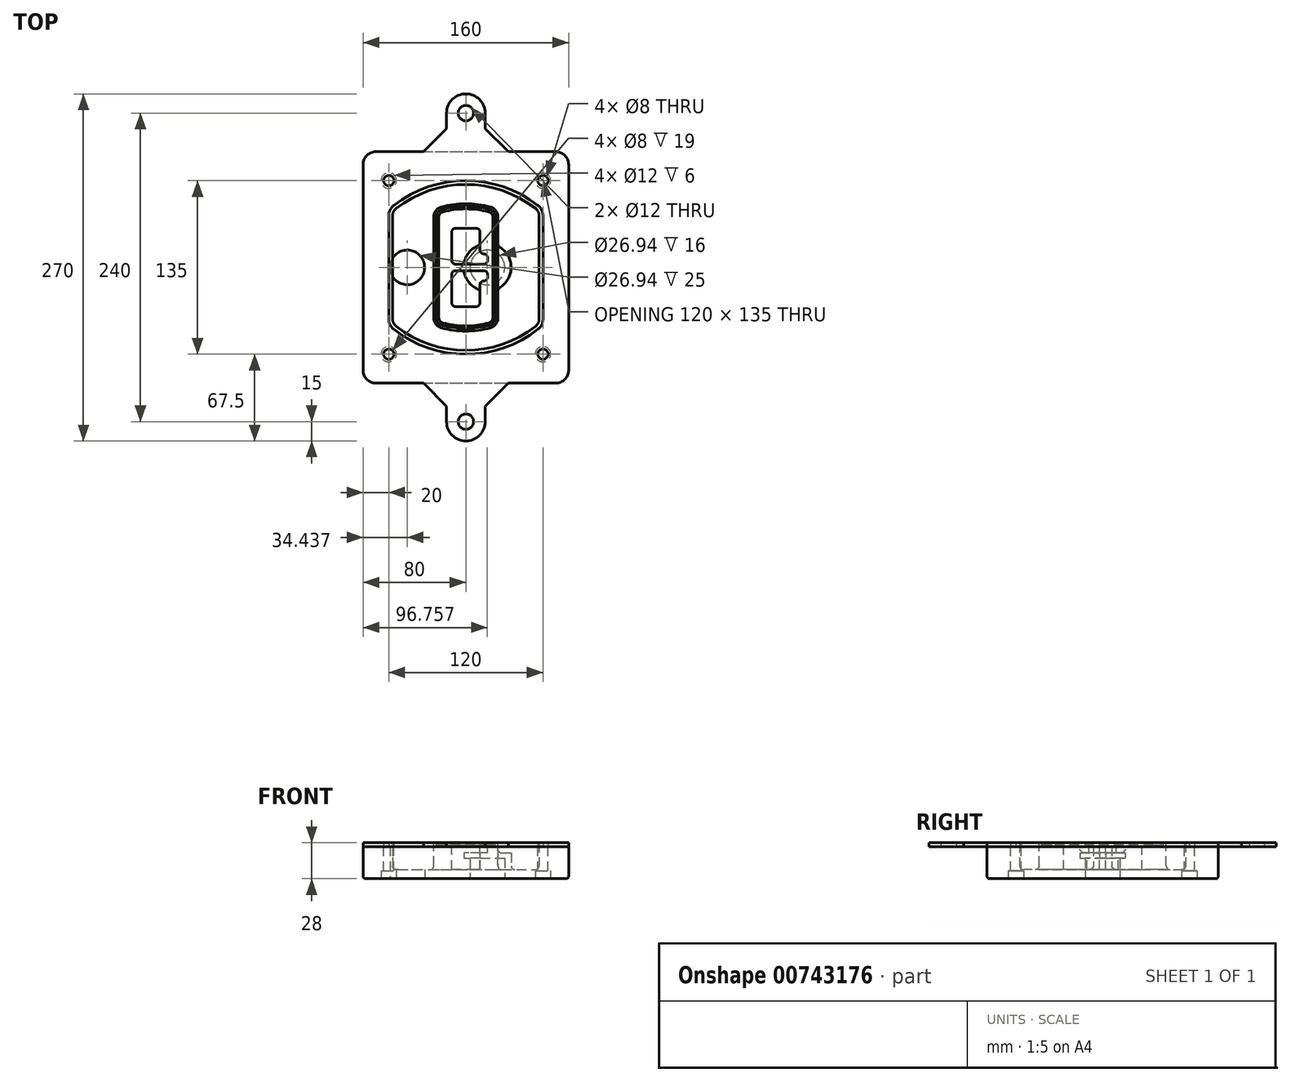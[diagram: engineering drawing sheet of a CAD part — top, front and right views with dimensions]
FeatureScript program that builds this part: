
annotation { "Feature Type Name" : "Feature", "Feature Type Description" : "" }
export const myFeature = defineFeature(function(context is Context, id is Id, definition is map)
    precondition{}
    {
        {
            var Q0;
            Q0=qCreatedBy(makeId("Top.planeOp"),FACE);
            var sketch = newSketch(context, id + "F0", { "sketchPlane" : qUnion([Q0])});
            skPoint(sketch, "E0.rect.middle", {"position": v(0, 0) * mm});
            skLineSegment(sketch, "E1.bottom", {"start": v(-70, -90) * mm, "end": v(70, -90) * mm});
            skLineSegment(sketch, "E1.top", {"start": v(-70, 90) * mm, "end": v(70, 90) * mm});
            skLineSegment(sketch, "E1.left", {"start": v(-80, -80) * mm, "end": v(-80, 80) * mm});
            skLineSegment(sketch, "E1.right", {"start": v(80, -80) * mm, "end": v(80, 80) * mm});
            skLineSegment(sketch, "E2", {"start": v(-80, 90) * mm, "end": v(80, -90) * mm, "construction": true});
            skLineSegment(sketch, "E3", {"start": v(80, 90) * mm, "end": v(-80, -90) * mm, "construction": true});
            skCircle(sketch, "E4", {"center": v(-60, 67.5) * mm, "radius": 4 * mm});
            skCircle(sketch, "E5", {"center": v(60, 67.5) * mm, "radius": 4 * mm});
            skCircle(sketch, "E6", {"center": v(60, -67.5) * mm, "radius": 4 * mm});
            skCircle(sketch, "E7", {"center": v(-60, -67.5) * mm, "radius": 4 * mm});
            skLineSegment(sketch, "E8", {"start": v(-60, 67.5) * mm, "end": v(60, 67.5) * mm, "construction": true});
            skLineSegment(sketch, "E9", {"start": v(60, 67.5) * mm, "end": v(60, -67.5) * mm, "construction": true});
            skLineSegment(sketch, "E10", {"start": v(60, -67.5) * mm, "end": v(-60, -67.5) * mm, "construction": true});
            skLineSegment(sketch, "E11", {"start": v(-60, -67.5) * mm, "end": v(-60, 67.5) * mm, "construction": true});
            skLineSegment(sketch, "E12", {"start": v(-60, 40.3) * mm, "end": v(-60, -40.3) * mm});
            skLineSegment(sketch, "E13", {"start": v(60, 40.3) * mm, "end": v(60, -40.3) * mm});
            skArc(sketch, "E14", {"start": v(56.15, 48.18) * mm, "mid": v(0, 67.5) * mm, "end": v(-56.15, 48.18) * mm});
            skArc(sketch, "E15", {"start": v(-56.15, -48.18) * mm, "mid": v(0, -67.5) * mm, "end": v(56.15, -48.18) * mm});
            skLineSegment(sketch, "E16", {"start": v(-60, 0) * mm, "end": v(60, 0) * mm, "construction": true});
            skPoint(sketch, "E17.visualSharp", {"position": v(-60, -45) * mm});
            skArc(sketch, "E17.filletArc", {"start": v(-60, -40.3) * mm, "mid": v(-58.99, -44.68) * mm, "end": v(-56.15, -48.18) * mm});
            skPoint(sketch, "E18.visualSharp", {"position": v(-60, 45) * mm});
            skArc(sketch, "E18.filletArc", {"start": v(-56.15, 48.18) * mm, "mid": v(-58.99, 44.68) * mm, "end": v(-60, 40.3) * mm});
            skPoint(sketch, "E19.visualSharp", {"position": v(60, 45) * mm});
            skArc(sketch, "E19.filletArc", {"start": v(60, 40.3) * mm, "mid": v(58.99, 44.68) * mm, "end": v(56.15, 48.18) * mm});
            skPoint(sketch, "E20.visualSharp", {"position": v(60, -45) * mm});
            skArc(sketch, "E20.filletArc", {"start": v(56.15, -48.18) * mm, "mid": v(58.99, -44.68) * mm, "end": v(60, -40.3) * mm});
            skPoint(sketch, "E21.visualSharp", {"position": v(-80, 90) * mm});
            skArc(sketch, "E21.filletArc", {"start": v(-70, 90) * mm, "mid": v(-77.07, 87.07) * mm, "end": v(-80, 80) * mm});
            skPoint(sketch, "E22.visualSharp", {"position": v(80, 90) * mm});
            skArc(sketch, "E22.filletArc", {"start": v(80, 80) * mm, "mid": v(77.07, 87.07) * mm, "end": v(70, 90) * mm});
            skPoint(sketch, "E23.visualSharp", {"position": v(80, -90) * mm});
            skArc(sketch, "E23.filletArc", {"start": v(70, -90) * mm, "mid": v(77.07, -87.07) * mm, "end": v(80, -80) * mm});
            skPoint(sketch, "E24.visualSharp", {"position": v(-80, -90) * mm});
            skArc(sketch, "E24.filletArc", {"start": v(-80, -80) * mm, "mid": v(-77.07, -87.07) * mm, "end": v(-70, -90) * mm});
            skArc(sketch, "E25.0", {"start": v(57, 40.3) * mm, "mid": v(56.3, 43.36) * mm, "end": v(54.3, 45.81) * mm});
            skLineSegment(sketch, "E25.1", {"start": v(57, 40.3) * mm, "end": v(57, -40.3) * mm});
            skArc(sketch, "E25.2", {"start": v(54.3, -45.81) * mm, "mid": v(56.3, -43.36) * mm, "end": v(57, -40.3) * mm});
            skArc(sketch, "E25.3", {"start": v(-54.3, -45.81) * mm, "mid": v(0, -64.5) * mm, "end": v(54.3, -45.81) * mm});
            skArc(sketch, "E25.4", {"start": v(-57, -40.3) * mm, "mid": v(-56.3, -43.36) * mm, "end": v(-54.3, -45.81) * mm});
            skArc(sketch, "E25.5", {"start": v(54.3, 45.81) * mm, "mid": v(0, 64.5) * mm, "end": v(-54.3, 45.81) * mm});
            skLineSegment(sketch, "E25.6", {"start": v(-57, 40.3) * mm, "end": v(-57, -40.3) * mm});
            skArc(sketch, "E25.7", {"start": v(-54.3, 45.81) * mm, "mid": v(-56.3, 43.36) * mm, "end": v(-57, 40.3) * mm});
            skArc(sketch, "E26.0", {"start": v(-58.62, 51.33) * mm, "mid": v(-62.58, 46.43) * mm, "end": v(-64, 40.3) * mm});
            skArc(sketch, "E26.1", {"start": v(58.62, 51.33) * mm, "mid": v(0, 71.5) * mm, "end": v(-58.62, 51.33) * mm});
            skArc(sketch, "E26.2", {"start": v(64, 40.3) * mm, "mid": v(62.58, 46.43) * mm, "end": v(58.62, 51.33) * mm});
            skLineSegment(sketch, "E26.3", {"start": v(64, 40.3) * mm, "end": v(64, -40.3) * mm});
            skArc(sketch, "E26.4", {"start": v(58.62, -51.33) * mm, "mid": v(62.58, -46.43) * mm, "end": v(64, -40.3) * mm});
            skLineSegment(sketch, "E26.5", {"start": v(-64, 40.3) * mm, "end": v(-64, -40.3) * mm});
            skArc(sketch, "E26.6", {"start": v(-58.62, -51.33) * mm, "mid": v(0, -71.5) * mm, "end": v(58.62, -51.33) * mm});
            skArc(sketch, "E26.7", {"start": v(-64, -40.3) * mm, "mid": v(-62.58, -46.43) * mm, "end": v(-58.62, -51.33) * mm});
            skSolve(sketch);
        }
        {
            var Q0;
            Q0=makeQuery(id+"F0.imprint","IMPRINT",FACE,{"disambiguationData":[TD([[makeQuery(id+"F0.imprint","IMPRINT",EDGE,{"derivedFrom":sQuery(id+"F0.wireOp",EDGE,"E1.bottom")}),1.0]])]});
            var Q1;
            Q1=makeQuery(id+"F0.imprint","IMPRINT",FACE,{"disambiguationData":[TD([[makeQuery(id+"F0.imprint","IMPRINT",EDGE,{"derivedFrom":sQuery(id+"F0.wireOp",EDGE,"E12")}),1.0]])]});
            var Q2;
            Q2=makeQuery(id+"F0.imprint","IMPRINT",FACE,{"disambiguationData":[TD([[makeQuery(id+"F0.imprint","IMPRINT",EDGE,{"derivedFrom":sQuery(id+"F0.wireOp",EDGE,"E25.0")}),1.0]])]});
            var Q3;
            Q3=makeQuery(id+"F0.imprint","IMPRINT",FACE,{"disambiguationData":[TD([[makeQuery(id+"F0.imprint","IMPRINT",EDGE,{"derivedFrom":sQuery(id+"F0.wireOp",EDGE,"E12")}),-1.0]])]});
            extrude(context, id + "F1", {"entities" : qUnion([Q0, Q1, Q2, Q3]), "oppositeDirection" : true, "depth" : 25 * mm});
        }
        {
            var Q0;
            Q0=makeQuery(id+"F0.imprint","IMPRINT",FACE,{"disambiguationData":[TD([[makeQuery(id+"F0.imprint","IMPRINT",EDGE,{"derivedFrom":sQuery(id+"F0.wireOp",EDGE,"E12")}),1.0]])]});
            extrude(context, id + "F2", {"entities" : qUnion([Q0]), "operationType" : NewBodyOperationType.ADD, "depth" : 3 * mm});
        }
        {
            var Q0;
            Q0=makeQuery(id+"F0.imprint","IMPRINT",FACE,{"disambiguationData":[TD([[makeQuery(id+"F0.imprint","IMPRINT",EDGE,{"derivedFrom":sQuery(id+"F0.wireOp",EDGE,"E25.0")}),1.0]])]});
            extrude(context, id + "F3", {"entities" : qUnion([Q0]), "operationType" : NewBodyOperationType.REMOVE, "oppositeDirection" : true, "depth" : 18 * mm});
        }
        {
            var Q0;
            Q0=makeQuery(id+"F2.opExtrude","CAP_FACE",FACE,{"disambiguationData":[OSD([sQuery(id+"F0.wireOp",EDGE,"E12"),sQuery(id+"F0.wireOp",EDGE,"E13"),sQuery(id+"F0.wireOp",EDGE,"E14"),sQuery(id+"F0.wireOp",EDGE,"E15"),sQuery(id+"F0.wireOp",EDGE,"E17.filletArc"),sQuery(id+"F0.wireOp",EDGE,"E18.filletArc"),sQuery(id+"F0.wireOp",EDGE,"E19.filletArc"),sQuery(id+"F0.wireOp",EDGE,"E20.filletArc"),sQuery(id+"F0.wireOp",EDGE,"E25.0"),sQuery(id+"F0.wireOp",EDGE,"E25.1"),sQuery(id+"F0.wireOp",EDGE,"E25.2"),sQuery(id+"F0.wireOp",EDGE,"E25.3"),sQuery(id+"F0.wireOp",EDGE,"E25.4"),sQuery(id+"F0.wireOp",EDGE,"E25.5"),sQuery(id+"F0.wireOp",EDGE,"E25.6"),sQuery(id+"F0.wireOp",EDGE,"E25.7")])],"isStart":false});
            var sketch = newSketch(context, id + "F4", { "sketchPlane" : qUnion([Q0])});
            skArc(sketch, "E27.0", {"start": v(-19.08, -46.97) * mm, "mid": v(0, -49.5) * mm, "end": v(19.08, -46.97) * mm});
            skArc(sketch, "E28.0", {"start": v(19.08, 46.97) * mm, "mid": v(0, 49.5) * mm, "end": v(-19.08, 46.97) * mm});
            skLineSegment(sketch, "E29", {"start": v(-25, 39.25) * mm, "end": v(-25, -39.25) * mm});
            skLineSegment(sketch, "E30", {"start": v(25, 39.25) * mm, "end": v(25, -39.25) * mm});
            skLineSegment(sketch, "E31", {"start": v(-25, 45.1) * mm, "end": v(25, 45.1) * mm, "construction": true});
            skLineSegment(sketch, "E32", {"start": v(-25, -45.1) * mm, "end": v(25, -45.1) * mm, "construction": true});
            skPoint(sketch, "E33.visualSharp", {"position": v(-25, 45.1) * mm});
            skArc(sketch, "E33.filletArc", {"start": v(-19.08, 46.97) * mm, "mid": v(-23.35, 44.11) * mm, "end": v(-25, 39.25) * mm});
            skPoint(sketch, "E34.visualSharp", {"position": v(25, 45.1) * mm});
            skArc(sketch, "E34.filletArc", {"start": v(25, 39.25) * mm, "mid": v(23.35, 44.11) * mm, "end": v(19.08, 46.97) * mm});
            skPoint(sketch, "E35.visualSharp", {"position": v(25, -45.1) * mm});
            skArc(sketch, "E35.filletArc", {"start": v(19.08, -46.97) * mm, "mid": v(23.35, -44.11) * mm, "end": v(25, -39.25) * mm});
            skPoint(sketch, "E36.visualSharp", {"position": v(-25, -45.1) * mm});
            skArc(sketch, "E36.filletArc", {"start": v(-25, -39.25) * mm, "mid": v(-23.35, -44.11) * mm, "end": v(-19.08, -46.97) * mm});
            skArc(sketch, "E37.0", {"start": v(54.3, 45.81) * mm, "mid": v(0, 64.5) * mm, "end": v(-54.3, 45.81) * mm});
            skArc(sketch, "E37.1", {"start": v(-54.3, 45.81) * mm, "mid": v(-56.3, 43.36) * mm, "end": v(-57, 40.3) * mm});
            skLineSegment(sketch, "E37.2", {"start": v(-57, 40.3) * mm, "end": v(-57, -40.3) * mm});
            skArc(sketch, "E37.3", {"start": v(-57, -40.3) * mm, "mid": v(-56.3, -43.36) * mm, "end": v(-54.3, -45.81) * mm});
            skArc(sketch, "E37.4", {"start": v(-54.3, -45.81) * mm, "mid": v(0, -64.5) * mm, "end": v(54.3, -45.81) * mm});
            skArc(sketch, "E37.5", {"start": v(54.3, -45.81) * mm, "mid": v(56.3, -43.36) * mm, "end": v(57, -40.3) * mm});
            skLineSegment(sketch, "E37.6", {"start": v(57, 40.3) * mm, "end": v(57, -40.3) * mm});
            skArc(sketch, "E37.7", {"start": v(57, 40.3) * mm, "mid": v(56.3, 43.36) * mm, "end": v(54.3, 45.81) * mm});
            skLineSegment(sketch, "E38.0", {"start": v(23, 39.25) * mm, "end": v(23, -39.25) * mm});
            skArc(sketch, "E38.1", {"start": v(18.56, -45.04) * mm, "mid": v(21.76, -42.9) * mm, "end": v(23, -39.25) * mm});
            skArc(sketch, "E38.2", {"start": v(-18.56, -45.04) * mm, "mid": v(0, -47.5) * mm, "end": v(18.56, -45.04) * mm});
            skArc(sketch, "E38.3", {"start": v(-23, -39.25) * mm, "mid": v(-21.76, -42.9) * mm, "end": v(-18.56, -45.04) * mm});
            skLineSegment(sketch, "E38.4", {"start": v(-23, 39.25) * mm, "end": v(-23, -39.25) * mm});
            skArc(sketch, "E38.5", {"start": v(23, 39.25) * mm, "mid": v(21.76, 42.9) * mm, "end": v(18.56, 45.04) * mm});
            skArc(sketch, "E38.6", {"start": v(-18.56, 45.04) * mm, "mid": v(-21.76, 42.9) * mm, "end": v(-23, 39.25) * mm});
            skArc(sketch, "E38.7", {"start": v(18.56, 45.04) * mm, "mid": v(0, 47.5) * mm, "end": v(-18.56, 45.04) * mm});
            skArc(sketch, "E39.0", {"start": v(21, 39.25) * mm, "mid": v(20.18, 41.68) * mm, "end": v(18.04, 43.1) * mm});
            skLineSegment(sketch, "E39.1", {"start": v(21, 39.25) * mm, "end": v(21, -39.25) * mm});
            skArc(sketch, "E39.2", {"start": v(18.04, -43.1) * mm, "mid": v(20.18, -41.68) * mm, "end": v(21, -39.25) * mm});
            skArc(sketch, "E39.3", {"start": v(-18.04, -43.1) * mm, "mid": v(0, -45.5) * mm, "end": v(18.04, -43.1) * mm});
            skArc(sketch, "E39.4", {"start": v(-21, -39.25) * mm, "mid": v(-20.18, -41.68) * mm, "end": v(-18.04, -43.1) * mm});
            skArc(sketch, "E39.5", {"start": v(18.04, 43.1) * mm, "mid": v(0, 45.5) * mm, "end": v(-18.04, 43.1) * mm});
            skLineSegment(sketch, "E39.6", {"start": v(-21, 39.25) * mm, "end": v(-21, -39.25) * mm});
            skArc(sketch, "E39.7", {"start": v(-18.04, 43.1) * mm, "mid": v(-20.18, 41.68) * mm, "end": v(-21, 39.25) * mm});
            skLineSegment(sketch, "E40", {"start": v(-25, 0) * mm, "end": v(25, 0) * mm, "construction": true});
            skLineSegment(sketch, "E41", {"start": v(-11, 5.5) * mm, "end": v(-11, 27.5) * mm});
            skLineSegment(sketch, "E42", {"start": v(-8, 30.5) * mm, "end": v(8, 30.5) * mm});
            skLineSegment(sketch, "E43", {"start": v(11, 27.5) * mm, "end": v(11, 13.5) * mm});
            skLineSegment(sketch, "E44", {"start": v(14, 10.5) * mm, "end": v(14, 10.5) * mm});
            skLineSegment(sketch, "E45", {"start": v(17, 7.5) * mm, "end": v(17, 5.5) * mm});
            skLineSegment(sketch, "E46", {"start": v(14, 2.5) * mm, "end": v(-8, 2.5) * mm});
            skPoint(sketch, "E47.visualSharp", {"position": v(-11, 30.5) * mm});
            skArc(sketch, "E47.filletArc", {"start": v(-8, 30.5) * mm, "mid": v(-10.12, 29.62) * mm, "end": v(-11, 27.5) * mm});
            skPoint(sketch, "E48.visualSharp", {"position": v(11, 30.5) * mm});
            skArc(sketch, "E48.filletArc", {"start": v(11, 27.5) * mm, "mid": v(10.12, 29.62) * mm, "end": v(8, 30.5) * mm});
            skPoint(sketch, "E49.visualSharp", {"position": v(11, 10.5) * mm});
            skArc(sketch, "E49.filletArc", {"start": v(11, 13.5) * mm, "mid": v(11.88, 11.38) * mm, "end": v(14, 10.5) * mm});
            skPoint(sketch, "E50.visualSharp", {"position": v(17, 10.5) * mm});
            skArc(sketch, "E50.filletArc", {"start": v(17, 7.5) * mm, "mid": v(16.12, 9.62) * mm, "end": v(14, 10.5) * mm});
            skPoint(sketch, "E51.visualSharp", {"position": v(17, 2.5) * mm});
            skArc(sketch, "E51.filletArc", {"start": v(14, 2.5) * mm, "mid": v(16.12, 3.38) * mm, "end": v(17, 5.5) * mm});
            skPoint(sketch, "E52.visualSharp", {"position": v(-11, 2.5) * mm});
            skArc(sketch, "E52.filletArc", {"start": v(-11, 5.5) * mm, "mid": v(-10.12, 3.38) * mm, "end": v(-8, 2.5) * mm});
            skLineSegment(sketch, "E53.0.MirrorCS", {"start": v(14, -2.5) * mm, "end": v(-8, -2.5) * mm});
            skArc(sketch, "E54.0.MirrorCS", {"start": v(-11, -5.5) * mm, "mid": v(-10.12, -3.38) * mm, "end": v(-8, -2.5) * mm});
            skLineSegment(sketch, "E55.0.MirrorCS", {"start": v(-11, -5.5) * mm, "end": v(-11, -27.5) * mm});
            skArc(sketch, "E56.0.MirrorCS", {"start": v(-8, -30.5) * mm, "mid": v(-10.12, -29.62) * mm, "end": v(-11, -27.5) * mm});
            skLineSegment(sketch, "E57.0.MirrorCS", {"start": v(-8, -30.5) * mm, "end": v(8, -30.5) * mm});
            skArc(sketch, "E58.0.MirrorCS", {"start": v(11, -27.5) * mm, "mid": v(10.12, -29.62) * mm, "end": v(8, -30.5) * mm});
            skLineSegment(sketch, "E59.0.MirrorCS", {"start": v(11, -27.5) * mm, "end": v(11, -13.5) * mm});
            skArc(sketch, "E60.0.MirrorCS", {"start": v(11, -13.5) * mm, "mid": v(11.88, -11.38) * mm, "end": v(14, -10.5) * mm});
            skArc(sketch, "E61.0.MirrorCS", {"start": v(17, -7.5) * mm, "mid": v(16.12, -9.62) * mm, "end": v(14, -10.5) * mm});
            skLineSegment(sketch, "E62.0.MirrorCS", {"start": v(17, -7.5) * mm, "end": v(17, -5.5) * mm});
            skArc(sketch, "E63.0.MirrorCS", {"start": v(14, -2.5) * mm, "mid": v(16.12, -3.38) * mm, "end": v(17, -5.5) * mm});
            skSolve(sketch);
        }
        {
            var Q0;
            Q0=makeQuery(id+"F4.imprint","IMPRINT",FACE,{"disambiguationData":[TD([[makeQuery(id+"F4.imprint","IMPRINT",EDGE,{"derivedFrom":sQuery(id+"F4.wireOp",EDGE,"E27.0")}),1.0]])]});
            var Q1;
            Q1=makeQuery(id+"F4.imprint","IMPRINT",FACE,{"disambiguationData":[TD([[makeQuery(id+"F4.imprint","IMPRINT",EDGE,{"derivedFrom":sQuery(id+"F4.wireOp",EDGE,"E38.0")}),-1.0]])]});
            var Q2;
            Q2=makeQuery(id+"F4.imprint","IMPRINT",FACE,{"disambiguationData":[TD([[makeQuery(id+"F4.imprint","IMPRINT",EDGE,{"derivedFrom":sQuery(id+"F4.wireOp",EDGE,"E39.0")}),1.0]])]});
            extrude(context, id + "F5", {"entities" : qUnion([Q0, Q1, Q2]), "operationType" : NewBodyOperationType.ADD, "endBound" : BoundingType.UP_TO_NEXT, "oppositeDirection" : true, "depth" : 25 * mm});
        }
        {
            var Q0;
            Q0=makeQuery(id+"F4.imprint","IMPRINT",FACE,{"disambiguationData":[TD([[makeQuery(id+"F4.imprint","IMPRINT",EDGE,{"derivedFrom":sQuery(id+"F4.wireOp",EDGE,"E38.0")}),-1.0]])]});
            extrude(context, id + "F6", {"entities" : qUnion([Q0]), "operationType" : NewBodyOperationType.REMOVE, "oppositeDirection" : true, "depth" : 2 * mm});
        }
        {
            var Q0;
            Q0=makeQuery(id+"F1.opExtrude","CAP_FACE",FACE,{"disambiguationData":[OSD([sQuery(id+"F0.wireOp",EDGE,"E1.bottom"),sQuery(id+"F0.wireOp",EDGE,"E1.top"),sQuery(id+"F0.wireOp",EDGE,"E1.left"),sQuery(id+"F0.wireOp",EDGE,"E1.right"),sQuery(id+"F0.wireOp",EDGE,"E4"),sQuery(id+"F0.wireOp",EDGE,"E5"),sQuery(id+"F0.wireOp",EDGE,"E6"),sQuery(id+"F0.wireOp",EDGE,"E7"),sQuery(id+"F0.wireOp",EDGE,"E21.filletArc"),sQuery(id+"F0.wireOp",EDGE,"E22.filletArc"),sQuery(id+"F0.wireOp",EDGE,"E23.filletArc"),sQuery(id+"F0.wireOp",EDGE,"E24.filletArc")])],"isStart":false});
            var sketch = newSketch(context, id + "F7", { "sketchPlane" : qUnion([Q0])});
            skCircle(sketch, "E64", {"center": v(16.76, 0) * mm, "radius": 13.47 * mm});
            skCircle(sketch, "E65", {"center": v(-45.56, 0) * mm, "radius": 13.47 * mm});
            skLineSegment(sketch, "E66", {"start": v(80, 0) * mm, "end": v(-80, 0) * mm});
            skCircle(sketch, "E67", {"center": v(16.76, 0) * mm, "radius": 18.47 * mm});
            skCircle(sketch, "E68", {"center": v(60, -67.5) * mm, "radius": 6 * mm});
            skCircle(sketch, "E69", {"center": v(-60, -67.5) * mm, "radius": 6 * mm});
            skCircle(sketch, "E70", {"center": v(-60, 67.5) * mm, "radius": 6 * mm});
            skCircle(sketch, "E71", {"center": v(60, 67.5) * mm, "radius": 6 * mm});
            skSolve(sketch);
        }
        {
            var Q0;
            {var subQ1=sQuery(id+"F7.wireOp",EDGE,"E66");var subQ4=sQuery(id+"F7.wireOp",EDGE,"E64");var subQ6=makeQuery(id+"F7.imprint","INTERSECT",VERTEX,{"disambiguationData":[OD(0.0)],"derivedFrom":[subQ4,subQ1]});Q0=makeQuery(id+"F7.imprint","IMPRINT",FACE,{"disambiguationData":[TD([[makeQuery(id+"F7.imprint","IMPRINT",EDGE,{"disambiguationData":[TD([[subQ6,-1.0]])],"derivedFrom":subQ4}),-1.0]])]});}
            var Q1;
            {var subQ0=sQuery(id+"F7.wireOp",EDGE,"E66");var subQ1=sQuery(id+"F7.wireOp",EDGE,"E64");var subQ3=makeQuery(id+"F7.imprint","INTERSECT",VERTEX,{"disambiguationData":[OD(0.0)],"derivedFrom":[subQ1,subQ0]});Q1=makeQuery(id+"F7.imprint","IMPRINT",FACE,{"disambiguationData":[TD([[makeQuery(id+"F7.imprint","IMPRINT",EDGE,{"disambiguationData":[TD([[subQ3,-1.0]])],"derivedFrom":subQ1}),1.0]])]});}
            var Q2;
            {var subQ0=sQuery(id+"F7.wireOp",EDGE,"E66");var subQ1=sQuery(id+"F7.wireOp",EDGE,"E64");var subQ3=makeQuery(id+"F7.imprint","INTERSECT",VERTEX,{"disambiguationData":[OD(0.0)],"derivedFrom":[subQ1,subQ0]});Q2=makeQuery(id+"F7.imprint","IMPRINT",FACE,{"disambiguationData":[TD([[makeQuery(id+"F7.imprint","IMPRINT",EDGE,{"disambiguationData":[TD([[subQ3,1.0]])],"derivedFrom":subQ1}),1.0]])]});}
            var Q3;
            {var subQ1=sQuery(id+"F7.wireOp",EDGE,"E66");var subQ4=sQuery(id+"F7.wireOp",EDGE,"E64");var subQ6=makeQuery(id+"F7.imprint","INTERSECT",VERTEX,{"disambiguationData":[OD(0.0)],"derivedFrom":[subQ4,subQ1]});Q3=makeQuery(id+"F7.imprint","IMPRINT",FACE,{"disambiguationData":[TD([[makeQuery(id+"F7.imprint","IMPRINT",EDGE,{"disambiguationData":[TD([[subQ6,1.0]])],"derivedFrom":subQ4}),-1.0]])]});}
            extrude(context, id + "F8", {"entities" : qUnion([Q0, Q1, Q2, Q3]), "operationType" : NewBodyOperationType.ADD, "oppositeDirection" : true, "depth" : 20 * mm});
        }
        {
            var Q0;
            {var subQ0=sQuery(id+"F7.wireOp",EDGE,"E66");var subQ1=sQuery(id+"F7.wireOp",EDGE,"E64");var subQ3=makeQuery(id+"F7.imprint","INTERSECT",VERTEX,{"disambiguationData":[OD(0.0)],"derivedFrom":[subQ1,subQ0]});Q0=makeQuery(id+"F7.imprint","IMPRINT",FACE,{"disambiguationData":[TD([[makeQuery(id+"F7.imprint","IMPRINT",EDGE,{"disambiguationData":[TD([[subQ3,-1.0]])],"derivedFrom":subQ1}),1.0]])]});}
            var Q1;
            {var subQ0=sQuery(id+"F7.wireOp",EDGE,"E66");var subQ1=sQuery(id+"F7.wireOp",EDGE,"E64");var subQ3=makeQuery(id+"F7.imprint","INTERSECT",VERTEX,{"disambiguationData":[OD(0.0)],"derivedFrom":[subQ1,subQ0]});Q1=makeQuery(id+"F7.imprint","IMPRINT",FACE,{"disambiguationData":[TD([[makeQuery(id+"F7.imprint","IMPRINT",EDGE,{"disambiguationData":[TD([[subQ3,1.0]])],"derivedFrom":subQ1}),1.0]])]});}
            extrude(context, id + "F9", {"entities" : qUnion([Q0, Q1]), "operationType" : NewBodyOperationType.REMOVE, "oppositeDirection" : true, "depth" : 16 * mm});
        }
        {
            var Q0;
            {var subQ0=sQuery(id+"F7.wireOp",EDGE,"E66");var subQ1=sQuery(id+"F7.wireOp",EDGE,"E65");var subQ3=makeQuery(id+"F7.imprint","INTERSECT",VERTEX,{"disambiguationData":[OD(0.0)],"derivedFrom":[subQ1,subQ0]});Q0=makeQuery(id+"F7.imprint","IMPRINT",FACE,{"disambiguationData":[TD([[makeQuery(id+"F7.imprint","IMPRINT",EDGE,{"disambiguationData":[TD([[subQ3,-1.0]])],"derivedFrom":subQ1}),1.0]])]});}
            var Q1;
            {var subQ0=sQuery(id+"F7.wireOp",EDGE,"E66");var subQ1=sQuery(id+"F7.wireOp",EDGE,"E65");var subQ3=makeQuery(id+"F7.imprint","INTERSECT",VERTEX,{"disambiguationData":[OD(0.0)],"derivedFrom":[subQ1,subQ0]});Q1=makeQuery(id+"F7.imprint","IMPRINT",FACE,{"disambiguationData":[TD([[makeQuery(id+"F7.imprint","IMPRINT",EDGE,{"disambiguationData":[TD([[subQ3,1.0]])],"derivedFrom":subQ1}),1.0]])]});}
            extrude(context, id + "F10", {"entities" : qUnion([Q0, Q1]), "operationType" : NewBodyOperationType.REMOVE, "oppositeDirection" : true, "depth" : 25 * mm});
        }
        {
            var Q0;
            Q0=makeQuery(id+"F7.imprint","IMPRINT",FACE,{"disambiguationData":[TD([[makeQuery(id+"F7.imprint","IMPRINT",EDGE,{"derivedFrom":sQuery(id+"F7.wireOp",EDGE,"E68")}),1.0]])]});
            var Q1;
            Q1=makeQuery(id+"F7.imprint","IMPRINT",FACE,{"disambiguationData":[TD([[makeQuery(id+"F7.imprint","IMPRINT",EDGE,{"derivedFrom":makeQuery(id+"F1.opExtrude","CAP_EDGE",EDGE,{"disambiguationData":[OSD([sQuery(id+"F0.wireOp",EDGE,"E5")])],"isStart":false})}),-1.0]])]});
            var Q2;
            Q2=makeQuery(id+"F7.imprint","IMPRINT",FACE,{"disambiguationData":[TD([[makeQuery(id+"F7.imprint","IMPRINT",EDGE,{"derivedFrom":sQuery(id+"F7.wireOp",EDGE,"E69")}),1.0]])]});
            var Q3;
            Q3=makeQuery(id+"F7.imprint","IMPRINT",FACE,{"disambiguationData":[TD([[makeQuery(id+"F7.imprint","IMPRINT",EDGE,{"derivedFrom":makeQuery(id+"F1.opExtrude","CAP_EDGE",EDGE,{"disambiguationData":[OSD([sQuery(id+"F0.wireOp",EDGE,"E4")])],"isStart":false})}),-1.0]])]});
            var Q4;
            Q4=makeQuery(id+"F7.imprint","IMPRINT",FACE,{"disambiguationData":[TD([[makeQuery(id+"F7.imprint","IMPRINT",EDGE,{"derivedFrom":sQuery(id+"F7.wireOp",EDGE,"E70")}),1.0]])]});
            var Q5;
            Q5=makeQuery(id+"F7.imprint","IMPRINT",FACE,{"disambiguationData":[TD([[makeQuery(id+"F7.imprint","IMPRINT",EDGE,{"derivedFrom":makeQuery(id+"F1.opExtrude","CAP_EDGE",EDGE,{"disambiguationData":[OSD([sQuery(id+"F0.wireOp",EDGE,"E7")])],"isStart":false})}),-1.0]])]});
            var Q6;
            Q6=makeQuery(id+"F7.imprint","IMPRINT",FACE,{"disambiguationData":[TD([[makeQuery(id+"F7.imprint","IMPRINT",EDGE,{"derivedFrom":sQuery(id+"F7.wireOp",EDGE,"E71")}),1.0]])]});
            var Q7;
            Q7=makeQuery(id+"F7.imprint","IMPRINT",FACE,{"disambiguationData":[TD([[makeQuery(id+"F7.imprint","IMPRINT",EDGE,{"derivedFrom":makeQuery(id+"F1.opExtrude","CAP_EDGE",EDGE,{"disambiguationData":[OSD([sQuery(id+"F0.wireOp",EDGE,"E6")])],"isStart":false})}),-1.0]])]});
            extrude(context, id + "F11", {"entities" : qUnion([Q0, Q1, Q2, Q3, Q4, Q5, Q6, Q7]), "operationType" : NewBodyOperationType.REMOVE, "oppositeDirection" : true, "depth" : 6 * mm});
        }
        {
            var Q0;
            Q0=makeQuery(id+"F9.boolean.opBoolean","COPY",FACE,{"derivedFrom":makeQuery(id+"F9.opExtrude","CAP_FACE",FACE,{"disambiguationData":[OSD([sQuery(id+"F7.wireOp",EDGE,"E64")])],"isStart":false})});
            var sketch = newSketch(context, id + "F12", { "sketchPlane" : qUnion([Q0])});
            skArc(sketch, "E72.0", {"start": v(11, 17.55) * mm, "mid": v(2.57, 11.82) * mm, "end": v(-1.54, 2.5) * mm});
            skArc(sketch, "E72.1", {"start": v(-1.54, -2.5) * mm, "mid": v(2.57, -11.82) * mm, "end": v(11, -17.55) * mm});
            skLineSegment(sketch, "E73", {"start": v(-1.54, -2.5) * mm, "end": v(14, -2.5) * mm});
            skLineSegment(sketch, "E74.0", {"start": v(14, 2.5) * mm, "end": v(-1.54, 2.5) * mm});
            skArc(sketch, "E74.1", {"start": v(14, 2.5) * mm, "mid": v(16.12, 3.38) * mm, "end": v(17, 5.5) * mm});
            skLineSegment(sketch, "E74.2", {"start": v(17, 7.5) * mm, "end": v(17, 5.5) * mm});
            skArc(sketch, "E74.3", {"start": v(17, 7.5) * mm, "mid": v(16.12, 9.62) * mm, "end": v(14, 10.5) * mm});
            skArc(sketch, "E74.4", {"start": v(11, 13.5) * mm, "mid": v(11.88, 11.38) * mm, "end": v(14, 10.5) * mm});
            skLineSegment(sketch, "E74.5", {"start": v(11, 17.55) * mm, "end": v(11, 13.5) * mm});
            skLineSegment(sketch, "E74.7", {"start": v(14, -2.5) * mm, "end": v(-1.54, -2.5) * mm});
            skArc(sketch, "E74.8", {"start": v(14, -2.5) * mm, "mid": v(16.12, -3.38) * mm, "end": v(17, -5.5) * mm});
            skLineSegment(sketch, "E74.9", {"start": v(17, -7.5) * mm, "end": v(17, -5.5) * mm});
            skArc(sketch, "E74.10", {"start": v(17, -7.5) * mm, "mid": v(16.12, -9.62) * mm, "end": v(14, -10.5) * mm});
            skArc(sketch, "E74.11", {"start": v(11, -13.5) * mm, "mid": v(11.88, -11.38) * mm, "end": v(14, -10.5) * mm});
            skLineSegment(sketch, "E74.12", {"start": v(11, -17.55) * mm, "end": v(11, -13.5) * mm});
            skPoint(sketch, "E75.orphan", {"position": v(11, -27.5) * mm});
            skPoint(sketch, "E76.orphan", {"position": v(-8, -2.5) * mm});
            skPoint(sketch, "E77.orphan", {"position": v(-8, 2.5) * mm});
            skPoint(sketch, "E78.orphan", {"position": v(11, 27.5) * mm});
            skSolve(sketch);
        }
        {
            var Q0;
            {var subQ7=sQuery(id+"F12.wireOp",EDGE,"E72.0");var subQ14=sQuery(id+"F12.wireOp",EDGE,"E72.1");var subQ16=sQuery(id+"F12.wireOp",EDGE,"E74.1");var subQ18=sQuery(id+"F12.wireOp",EDGE,"E74.8");Q0=qUnion([makeQuery(id+"F12.imprint","IMPRINT",FACE,{"disambiguationData":[TD([[makeQuery(id+"F12.imprint","IMPRINT",EDGE,{"derivedFrom":subQ7}),1.0]])]}),makeQuery(id+"F12.imprint","IMPRINT",FACE,{"disambiguationData":[TD([[makeQuery(id+"F12.imprint","IMPRINT",EDGE,{"derivedFrom":subQ14}),1.0]])]}),makeQuery(id+"F12.imprint","IMPRINT",FACE,{"disambiguationData":[TD([[makeQuery(id+"F12.imprint","IMPRINT",EDGE,{"derivedFrom":subQ16}),1.0]])]}),makeQuery(id+"F12.imprint","IMPRINT",FACE,{"disambiguationData":[TD([[makeQuery(id+"F12.imprint","IMPRINT",EDGE,{"derivedFrom":subQ18}),-1.0]])]})]);}
            var Q1;
            Q1=makeQuery(id+"F5.boolean.opBoolean","SPLIT",FACE,{"disambiguationData":[TD([makeQuery(id+"F5.opExtrude","SWEPT_FACE",FACE,{"disambiguationData":[OSD([sQuery(id+"F4.wireOp",EDGE,"E41")])]})])],"derivedFrom":makeQuery(id+"F3.boolean.opBoolean","COPY",FACE,{"derivedFrom":makeQuery(id+"F3.opExtrude","CAP_FACE",FACE,{"disambiguationData":[OSD([sQuery(id+"F0.wireOp",EDGE,"E25.0"),sQuery(id+"F0.wireOp",EDGE,"E25.1"),sQuery(id+"F0.wireOp",EDGE,"E25.2"),sQuery(id+"F0.wireOp",EDGE,"E25.3"),sQuery(id+"F0.wireOp",EDGE,"E25.4"),sQuery(id+"F0.wireOp",EDGE,"E25.5"),sQuery(id+"F0.wireOp",EDGE,"E25.6"),sQuery(id+"F0.wireOp",EDGE,"E25.7")])],"isStart":false})})});
            extrude(context, id + "F13", {"entities" : qUnion([Q0]), "operationType" : NewBodyOperationType.REMOVE, "endBound" : BoundingType.UP_TO_SURFACE, "endBoundEntityFace" : qUnion([Q1]), "depth" : 25 * mm});
        }
        {
            var Q0;
            Q0=makeQuery(id+"F3.boolean.opBoolean","COPY",EDGE,{"derivedFrom":makeQuery(id+"F3.opExtrude","CAP_EDGE",EDGE,{"disambiguationData":[OSD([sQuery(id+"F0.wireOp",EDGE,"E25.6")])],"isStart":false})});
            var Q1;
            Q1=makeQuery(id+"F8.boolean.opBoolean","INTERSECT",EDGE,{"derivedFrom":[makeQuery(id+"F5.opExtrude","SWEPT_FACE",FACE,{"disambiguationData":[OSD([sQuery(id+"F4.wireOp",EDGE,"E30")])]}),makeQuery(id+"F8.opExtrude","CAP_FACE",FACE,{"disambiguationData":[OSD([sQuery(id+"F7.wireOp",EDGE,"E67")])],"isStart":false})]});
            var Q2;
            Q2=makeQuery(id+"F8.boolean.opBoolean","INTERSECT",EDGE,{"disambiguationData":[OD(1.0)],"derivedFrom":[makeQuery(id+"F5.opExtrude","SWEPT_FACE",FACE,{"disambiguationData":[OSD([sQuery(id+"F4.wireOp",EDGE,"E30")])]}),makeQuery(id+"F8.opExtrude","SWEPT_FACE",FACE,{"disambiguationData":[OSD([sQuery(id+"F7.wireOp",EDGE,"E67")])]})]});
            var Q3;
            {var subQ0=sQuery(id+"F4.wireOp",EDGE,"E30");Q3=makeQuery(id+"F8.boolean.opBoolean","SPLIT",EDGE,{"disambiguationData":[TD([makeQuery(id+"F5.opExtrude","SWEPT_FACE",FACE,{"disambiguationData":[OSD([sQuery(id+"F4.wireOp",EDGE,"E35.filletArc")])]})])],"derivedFrom":makeQuery(id+"F5.opExtrude","CAP_EDGE",EDGE,{"disambiguationData":[OSD([subQ0])],"isStart":false})});}
            var Q4;
            {var subQ0=sQuery(id+"F0.wireOp",EDGE,"E25.7");var subQ1=sQuery(id+"F0.wireOp",EDGE,"E25.1");var subQ2=sQuery(id+"F0.wireOp",EDGE,"E25.6");var subQ3=sQuery(id+"F0.wireOp",EDGE,"E25.5");var subQ4=sQuery(id+"F0.wireOp",EDGE,"E25.4");var subQ5=sQuery(id+"F0.wireOp",EDGE,"E25.0");var subQ6=sQuery(id+"F0.wireOp",EDGE,"E25.2");var subQ7=sQuery(id+"F0.wireOp",EDGE,"E25.3");Q4=makeQuery(id+"F8.boolean.opBoolean","INTERSECT",EDGE,{"derivedFrom":[makeQuery(id+"F5.boolean.opBoolean","SPLIT",FACE,{"disambiguationData":[TD([makeQuery(id+"F2.opExtrude","SWEPT_FACE",FACE,{"disambiguationData":[OSD([subQ5])]})])],"derivedFrom":makeQuery(id+"F3.boolean.opBoolean","COPY",FACE,{"derivedFrom":makeQuery(id+"F3.opExtrude","CAP_FACE",FACE,{"disambiguationData":[OSD([subQ5,subQ1,subQ6,subQ7,subQ4,subQ3,subQ2,subQ0])],"isStart":false})})}),makeQuery(id+"F8.opExtrude","SWEPT_FACE",FACE,{"disambiguationData":[OSD([sQuery(id+"F7.wireOp",EDGE,"E67")])]})]});}
            var Q5;
            Q5=makeQuery(id+"F8.boolean.opBoolean","INTERSECT",EDGE,{"disambiguationData":[OD(0.0)],"derivedFrom":[makeQuery(id+"F5.opExtrude","SWEPT_FACE",FACE,{"disambiguationData":[OSD([sQuery(id+"F4.wireOp",EDGE,"E30")])]}),makeQuery(id+"F8.opExtrude","SWEPT_FACE",FACE,{"disambiguationData":[OSD([sQuery(id+"F7.wireOp",EDGE,"E67")])]})]});
            fillet(context, id + "F14", {"entities" : qUnion([Q0, Q1, Q2, Q3, Q4, Q5]), "radius" : 3 * mm, "tangentPropagation" : true, "allowEdgeOverflow" : false});
        }
        {
            var Q0;
            Q0=makeQuery(id+"F1.opExtrude","CAP_EDGE",EDGE,{"disambiguationData":[OSD([sQuery(id+"F0.wireOp",EDGE,"E1.bottom")])],"isStart":false});
            fillet(context, id + "F15", {"entities" : qUnion([Q0]), "radius" : 2 * mm, "tangentPropagation" : true, "allowEdgeOverflow" : false});
        }
        {
            var Q0;
            {var subQ0=sQuery(id+"F0.wireOp",EDGE,"E21.filletArc");var subQ1=sQuery(id+"F0.wireOp",EDGE,"E7");var subQ2=sQuery(id+"F0.wireOp",EDGE,"E6");var subQ3=sQuery(id+"F0.wireOp",EDGE,"E5");var subQ4=sQuery(id+"F0.wireOp",EDGE,"E4");var subQ5=sQuery(id+"F0.wireOp",EDGE,"E22.filletArc");var subQ6=sQuery(id+"F0.wireOp",EDGE,"E1.bottom");var subQ7=sQuery(id+"F0.wireOp",EDGE,"E1.right");var subQ8=sQuery(id+"F0.wireOp",EDGE,"E1.top");var subQ9=sQuery(id+"F0.wireOp",EDGE,"E1.left");var subQ10=sQuery(id+"F0.wireOp",EDGE,"E23.filletArc");var subQ11=sQuery(id+"F0.wireOp",EDGE,"E24.filletArc");Q0=makeQuery(id+"F2.boolean.opBoolean","SPLIT",FACE,{"disambiguationData":[TD([makeQuery(id+"F1.opExtrude","SWEPT_FACE",FACE,{"disambiguationData":[OSD([subQ6])]})])],"derivedFrom":makeQuery(id+"F1.opExtrude","CAP_FACE",FACE,{"disambiguationData":[OSD([subQ6,subQ8,subQ9,subQ7,subQ4,subQ3,subQ2,subQ1,subQ0,subQ5,subQ10,subQ11])],"isStart":true})});}
            var sketch = newSketch(context, id + "F16", { "sketchPlane" : qUnion([Q0])});
            skLineSegment(sketch, "E79.0", {"start": v(-70, 90) * mm, "end": v(70, 90) * mm});
            skArc(sketch, "E79.1", {"start": v(-70, 90) * mm, "mid": v(-77.07, 87.07) * mm, "end": v(-80, 80) * mm});
            skLineSegment(sketch, "E79.2", {"start": v(-80, -80) * mm, "end": v(-80, 80) * mm});
            skCircle(sketch, "E79.3", {"center": v(-60, 67.5) * mm, "radius": 4 * mm});
            skArc(sketch, "E79.4", {"start": v(56.15, 48.18) * mm, "mid": v(0, 67.5) * mm, "end": v(-56.15, 48.18) * mm});
            skLineSegment(sketch, "E79.5", {"start": v(-60, 40.3) * mm, "end": v(-60, -40.3) * mm});
            skArc(sketch, "E79.6", {"start": v(-56.15, 48.18) * mm, "mid": v(-58.99, 44.68) * mm, "end": v(-60, 40.3) * mm});
            skArc(sketch, "E79.7", {"start": v(60, 40.3) * mm, "mid": v(58.99, 44.68) * mm, "end": v(56.15, 48.18) * mm});
            skLineSegment(sketch, "E79.8", {"start": v(60, 40.3) * mm, "end": v(60, -40.3) * mm});
            skCircle(sketch, "E79.9", {"center": v(60, 67.5) * mm, "radius": 4 * mm});
            skLineSegment(sketch, "E79.10", {"start": v(80, -80) * mm, "end": v(80, 80) * mm});
            skArc(sketch, "E79.11", {"start": v(80, 80) * mm, "mid": v(77.07, 87.07) * mm, "end": v(70, 90) * mm});
            skArc(sketch, "E79.12", {"start": v(70, -90) * mm, "mid": v(77.07, -87.07) * mm, "end": v(80, -80) * mm});
            skLineSegment(sketch, "E79.13", {"start": v(-70, -90) * mm, "end": v(70, -90) * mm});
            skCircle(sketch, "E79.14", {"center": v(60, -67.5) * mm, "radius": 4 * mm});
            skArc(sketch, "E79.15", {"start": v(56.15, -48.18) * mm, "mid": v(58.99, -44.68) * mm, "end": v(60, -40.3) * mm});
            skArc(sketch, "E79.16", {"start": v(-56.15, -48.18) * mm, "mid": v(0, -67.5) * mm, "end": v(56.15, -48.18) * mm});
            skArc(sketch, "E79.17", {"start": v(-60, -40.3) * mm, "mid": v(-58.99, -44.68) * mm, "end": v(-56.15, -48.18) * mm});
            skCircle(sketch, "E79.18", {"center": v(-60, -67.5) * mm, "radius": 4 * mm});
            skArc(sketch, "E79.19", {"start": v(-80, -80) * mm, "mid": v(-77.07, -87.07) * mm, "end": v(-70, -90) * mm});
            skLineSegment(sketch, "E80", {"start": v(0, 90) * mm, "end": v(0, 120) * mm, "construction": true});
            skCircle(sketch, "E81", {"center": v(0, 120) * mm, "radius": 6 * mm});
            skLineSegment(sketch, "E82", {"start": v(-33, 90) * mm, "end": v(-15, 108) * mm});
            skLineSegment(sketch, "E83", {"start": v(-15, 108) * mm, "end": v(-15, 120) * mm});
            skArc(sketch, "E84", {"start": v(-15, 120) * mm, "mid": v(0, 135) * mm, "end": v(15, 120) * mm});
            skLineSegment(sketch, "E85", {"start": v(15, 120) * mm, "end": v(15, 108) * mm});
            skLineSegment(sketch, "E86", {"start": v(-80, 0) * mm, "end": v(80, 0) * mm, "construction": true});
            skLineSegment(sketch, "E87", {"start": v(15, 108) * mm, "end": v(33, 90) * mm});
            skLineSegment(sketch, "E88.MirrorCS", {"start": v(15, -108) * mm, "end": v(33, -90) * mm});
            skLineSegment(sketch, "E89.MirrorCS", {"start": v(15, -120) * mm, "end": v(15, -108) * mm});
            skArc(sketch, "E90.MirrorCS", {"start": v(-15, -120) * mm, "mid": v(0, -135) * mm, "end": v(15, -120) * mm});
            skCircle(sketch, "E91.MirrorC", {"center": v(0, -120) * mm, "radius": 6 * mm});
            skLineSegment(sketch, "E92.MirrorCS", {"start": v(-15, -108) * mm, "end": v(-15, -120) * mm});
            skLineSegment(sketch, "E93.MirrorCS", {"start": v(-33, -90) * mm, "end": v(-15, -108) * mm});
            skSolve(sketch);
        }
        {
            var Q0;
            Q0=makeQuery(id+"F16.imprint","IMPRINT",FACE,{"disambiguationData":[TD([[makeQuery(id+"F16.imprint","IMPRINT",EDGE,{"derivedFrom":sQuery(id+"F16.wireOp",EDGE,"E81")}),-1.0]])]});
            var Q1;
            {var subQ6=sQuery(id+"F16.wireOp",EDGE,"E79.1");Q1=makeQuery(id+"F16.imprint","IMPRINT",FACE,{"disambiguationData":[TD([[makeQuery(id+"F16.imprint","IMPRINT",EDGE,{"derivedFrom":subQ6}),1.0]])]});}
            var Q2;
            {var subQ0=sQuery(id+"F16.wireOp",EDGE,"E88.MirrorCS");Q2=makeQuery(id+"F16.imprint","IMPRINT",FACE,{"disambiguationData":[TD([[makeQuery(id+"F16.imprint","IMPRINT",EDGE,{"derivedFrom":subQ0}),1.0]])]});}
            var Q3;
            Q3=makeQuery(id+"F2.opExtrude","CAP_FACE",FACE,{"disambiguationData":[OSD([sQuery(id+"F0.wireOp",EDGE,"E12"),sQuery(id+"F0.wireOp",EDGE,"E13"),sQuery(id+"F0.wireOp",EDGE,"E14"),sQuery(id+"F0.wireOp",EDGE,"E15"),sQuery(id+"F0.wireOp",EDGE,"E17.filletArc"),sQuery(id+"F0.wireOp",EDGE,"E18.filletArc"),sQuery(id+"F0.wireOp",EDGE,"E19.filletArc"),sQuery(id+"F0.wireOp",EDGE,"E20.filletArc"),sQuery(id+"F0.wireOp",EDGE,"E25.0"),sQuery(id+"F0.wireOp",EDGE,"E25.1"),sQuery(id+"F0.wireOp",EDGE,"E25.2"),sQuery(id+"F0.wireOp",EDGE,"E25.3"),sQuery(id+"F0.wireOp",EDGE,"E25.4"),sQuery(id+"F0.wireOp",EDGE,"E25.5"),sQuery(id+"F0.wireOp",EDGE,"E25.6"),sQuery(id+"F0.wireOp",EDGE,"E25.7")])],"isStart":false});
            extrude(context, id + "F17", {"entities" : qUnion([Q0, Q1, Q2]), "endBound" : BoundingType.UP_TO_SURFACE, "depth" : 25 * mm, "endBoundEntityFace" : qUnion([Q3]), "offsetDistance" : 25 * mm});
        }
    });
